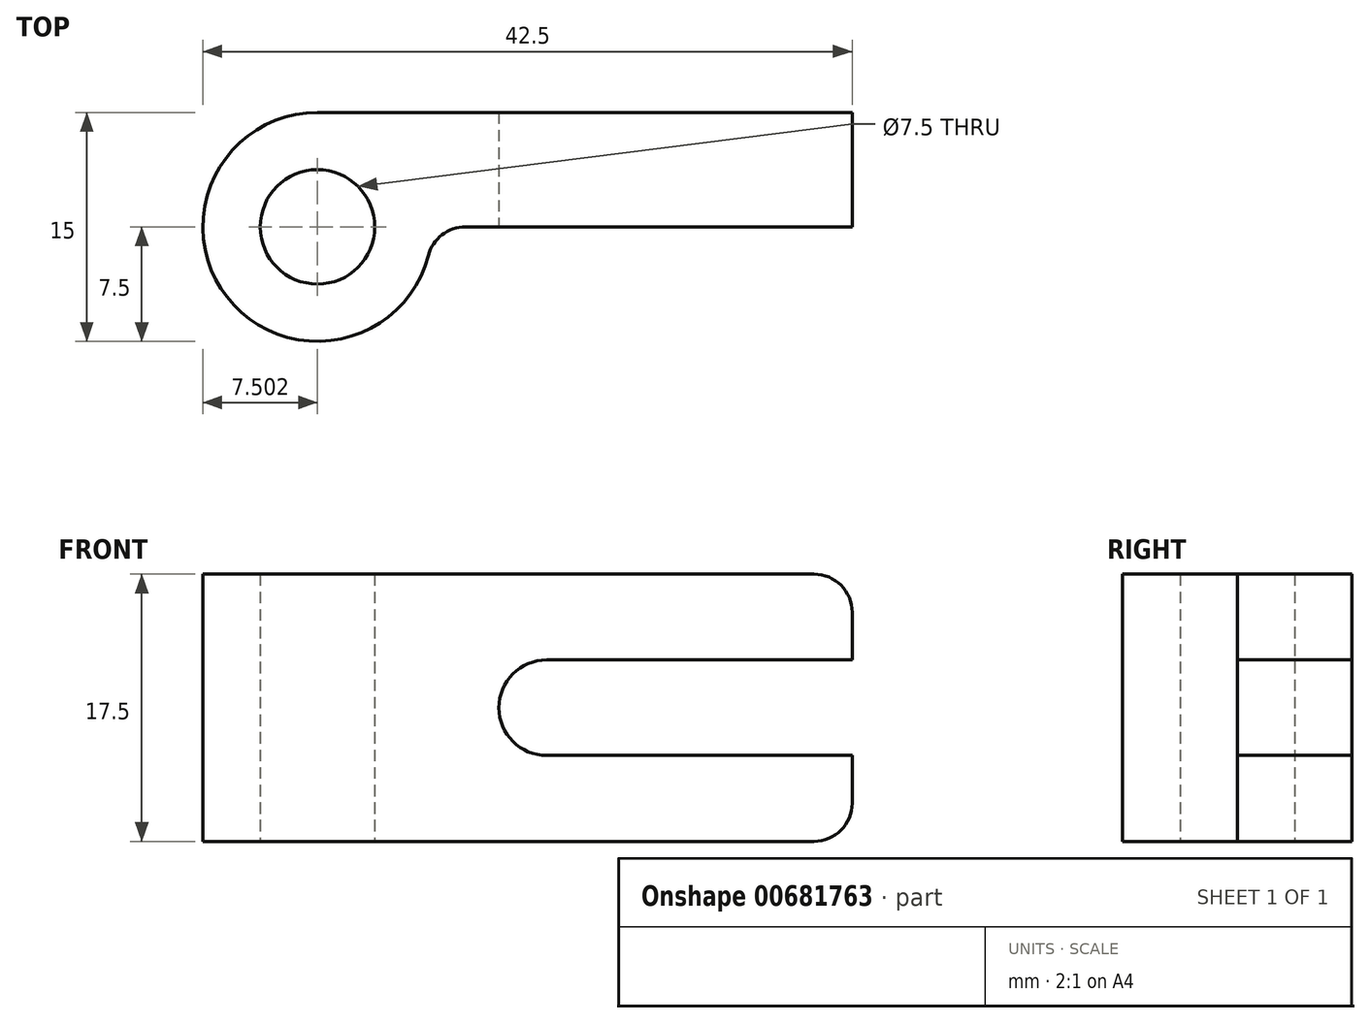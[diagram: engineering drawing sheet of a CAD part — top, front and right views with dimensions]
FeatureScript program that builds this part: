
annotation { "Feature Type Name" : "Feature", "Feature Type Description" : "" }
export const myFeature = defineFeature(function(context is Context, id is Id, definition is map)
    precondition{}
    {
        {
            var Q0;
            Q0=qCreatedBy(makeId("Top.planeOp"),FACE);
            var sketch = newSketch(context, id + "F0", { "sketchPlane" : qUnion([Q0])});
            skCircle(sketch, "E0", {"center": v(-40.67, 0) * mm, "radius": 3.75 * mm});
            skCircle(sketch, "E1", {"center": v(-40.67, 0) * mm, "radius": 7.5 * mm});
            skLineSegment(sketch, "E2", {"start": v(-40.67, 7.5) * mm, "end": v(-5.67, 7.5) * mm});
            skLineSegment(sketch, "E3", {"start": v(-5.67, 7.5) * mm, "end": v(-5.67, 0) * mm});
            skLineSegment(sketch, "E4", {"start": v(-5.67, 0) * mm, "end": v(-33.17, 0) * mm});
            skPoint(sketch, "E5", {"position": v(-25.67, 7.5) * mm});
            skSolve(sketch);
        }
        {
            var Q0;
            Q0 = qSketchRegion(id + "F0", true);
            extrude(context, id + "F1", {"entities" : qUnion([Q0]), "depth" : 17.5 * mm, "offsetDistance" : 25 * mm});
        }
        {
            var Q0;
            Q0=makeQuery(id+"F1.opExtrude","SWEPT_FACE",FACE,{"disambiguationData":[OSD([sQuery(id+"F0.wireOp",EDGE,"E4")])]});
            var sketch = newSketch(context, id + "F2", { "sketchPlane" : qUnion([Q0])});
            skLineSegment(sketch, "E6", {"start": v(-5.67, 11.88) * mm, "end": v(-25.67, 11.88) * mm});
            skLineSegment(sketch, "E7", {"start": v(-25.67, 5.63) * mm, "end": v(-5.67, 5.63) * mm});
            skArc(sketch, "E8", {"start": v(-25.67, 11.88) * mm, "mid": v(-28.8, 8.75) * mm, "end": v(-25.67, 5.63) * mm});
            skPoint(sketch, "E9.end.orphan", {"position": v(-25.67, 0) * mm});
            skSolve(sketch);
        }
        {
            var Q0;
            {var subQ0=sQuery(id+"F2.wireOp",EDGE,"E6");Q0=makeQuery(id+"F2.imprint","IMPRINT",FACE,{"disambiguationData":[TD([[makeQuery(id+"F2.imprint","IMPRINT",EDGE,{"derivedFrom":subQ0}),1.0]])]});}
            extrude(context, id + "F3", {"entities" : qUnion([Q0]), "operationType" : NewBodyOperationType.REMOVE, "oppositeDirection" : true, "depth" : 25 * mm, "offsetDistance" : 25 * mm});
        }
        {
            var Q0;
            Q0=makeQuery(id+"F1.opExtrude","CAP_EDGE",EDGE,{"disambiguationData":[OSD([sQuery(id+"F0.wireOp",EDGE,"E3")])],"isStart":false});
            var Q1;
            Q1=makeQuery(id+"F1.opExtrude","CAP_EDGE",EDGE,{"disambiguationData":[OSD([sQuery(id+"F0.wireOp",EDGE,"E3")])],"isStart":true});
            var Q2;
            Q2=makeQuery(id+"F1.opExtrude","SWEPT_EDGE",EDGE,{"disambiguationData":[OSD([sQuery(id+"F0.wireOp",EDGE,"E1"),sQuery(id+"F0.wireOp",EDGE,"E4")])]});
            fillet(context, id + "F4", {"entities" : qUnion([Q0, Q1, Q2]), "radius" : 2.5 * mm, "tangentPropagation" : true, "allowEdgeOverflow" : false});
        }
    });
